annotation { "Feature Type Name" : "Feature", "Feature Type Description" : "" }
export const myFeature = defineFeature(function(context is Context, id is Id, definition is map)
    precondition{}
    {
        {
            var Q0;
            Q0=qCreatedBy(makeId("Top.planeOp"),FACE);
            var sketch = newSketch(context, id + "F0", { "sketchPlane" : qUnion([Q0])});
            skLineSegment(sketch, "E0.bottom", {"start": v(-155.39, 132.34) * mm, "end": v(174.81, 132.34) * mm});
            skLineSegment(sketch, "E0.top", {"start": v(-155.39, -96.26) * mm, "end": v(174.81, -96.26) * mm});
            skLineSegment(sketch, "E0.left", {"start": v(-155.39, 132.34) * mm, "end": v(-155.39, -96.26) * mm});
            skLineSegment(sketch, "E0.right", {"start": v(174.81, 132.34) * mm, "end": v(174.81, -96.26) * mm});
            skCircle(sketch, "E1", {"center": v(-140.15, 117.1) * mm, "radius": 4 * mm});
            skCircle(sketch, "E2", {"center": v(-38.55, 117.1) * mm, "radius": 4 * mm});
            skCircle(sketch, "E3", {"center": v(57.97, 116.69) * mm, "radius": 4 * mm});
            skCircle(sketch, "E4", {"center": v(159.57, 117.1) * mm, "radius": 4 * mm});
            skCircle(sketch, "E5", {"center": v(-140.15, 18.04) * mm, "radius": 4 * mm});
            skCircle(sketch, "E6", {"center": v(-140.15, -58.16) * mm, "radius": 4 * mm});
            skCircle(sketch, "E7", {"center": v(159.57, 18.04) * mm, "radius": 4 * mm});
            skCircle(sketch, "E8", {"center": v(159.57, -58.16) * mm, "radius": 4 * mm});
            skCircle(sketch, "E9", {"center": v(-89.35, -81.02) * mm, "radius": 4 * mm});
            skCircle(sketch, "E10", {"center": v(9.71, -81.02) * mm, "radius": 4.44 * mm});
            skCircle(sketch, "E11", {"center": v(108.77, -81.02) * mm, "radius": 4 * mm});
            skCircle(sketch, "E12", {"center": v(-142.69, -83.56) * mm, "radius": 6.35 * mm});
            skCircle(sketch, "E13", {"center": v(162.11, -83.56) * mm, "radius": 6.35 * mm});
            skText(sketch, "E14", { "text": "CULTUR", "fontName": "RobotoSlab-Regular.ttf"});
            skText(sketch, "E15", { "text": "SUP FISHING", "fontName": "Tinos-Bold.ttf"});
            const initialGuessF0  = {"E14": [-0.08375, 0, 1, 0, 0.02933], "E15": [-0.07246, -0.02336, 1, 0, 0.0163]};
            skSetInitialGuess(sketch, initialGuessF0);
            skSolve(sketch);
        }
        {
            var Q0;
            Q0=makeQuery(id+"F0.imprint","IMPRINT",FACE,{"disambiguationData":[TD([[makeQuery(id+"F0.imprint","IMPRINT",EDGE,{"derivedFrom":sQuery(id+"F0.wireOp",EDGE,"E0.bottom")}),-1.0]])]});
            extrude(context, id + "F1", {"entities" : qUnion([Q0]), "endBound" : BoundingType.SYMMETRIC, "depth" : 12.7 * mm, "offsetDistance" : 25.4 * mm});
        }
        {
            var Q0;
            Q0=makeQuery(id+"F1.opExtrude","SWEPT_EDGE",EDGE,{"disambiguationData":[OSD([sQuery(id+"F0.wireOp",EDGE,"E0.top"),sQuery(id+"F0.wireOp",EDGE,"E0.left")])]});
            var Q1;
            Q1=makeQuery(id+"F1.opExtrude","SWEPT_EDGE",EDGE,{"disambiguationData":[OSD([sQuery(id+"F0.wireOp",EDGE,"E0.top"),sQuery(id+"F0.wireOp",EDGE,"E0.right")])]});
            var Q2;
            Q2=makeQuery(id+"F1.opExtrude","SWEPT_EDGE",EDGE,{"disambiguationData":[OSD([sQuery(id+"F0.wireOp",EDGE,"E0.bottom"),sQuery(id+"F0.wireOp",EDGE,"E0.right")])]});
            var Q3;
            Q3=makeQuery(id+"F1.opExtrude","SWEPT_EDGE",EDGE,{"disambiguationData":[OSD([sQuery(id+"F0.wireOp",EDGE,"E0.bottom"),sQuery(id+"F0.wireOp",EDGE,"E0.left")])]});
            fillet(context, id + "F2", {"entities" : qUnion([Q0, Q1, Q2, Q3]), "radius" : 5.08 * mm, "tangentPropagation" : true, "allowEdgeOverflow" : false});
        }
        {
            var Q0;
            Q0=makeQuery(id+"F1.opExtrude","CAP_EDGE",EDGE,{"disambiguationData":[OSD([sQuery(id+"F0.wireOp",EDGE,"E12")])],"isStart":false});
            var Q1;
            Q1=makeQuery(id+"F1.opExtrude","CAP_EDGE",EDGE,{"disambiguationData":[OSD([sQuery(id+"F0.wireOp",EDGE,"E13")])],"isStart":false});
            chamfer(context, id + "F3", {"entities" : qUnion([Q0, Q1]), "width" : 1.27 * mm, "tangentPropagation" : true});
        }
        {
            var Q0;
            Q0=qCreatedBy(makeId("Front.planeOp"),FACE);
            var sketch = newSketch(context, id + "F4", { "sketchPlane" : qUnion([Q0])});
            skLineSegment(sketch, "E16.bottom", {"start": v(139.7, 89.76) * mm, "end": v(98.1, 89.76) * mm});
            skLineSegment(sketch, "E16.top", {"start": v(139.7, 134.21) * mm, "end": v(-139.7, 134.21) * mm});
            skLineSegment(sketch, "E16.left", {"start": v(139.7, 89.76) * mm, "end": v(139.7, 134.21) * mm});
            skLineSegment(sketch, "E16.right", {"start": v(-139.7, 89.76) * mm, "end": v(-139.7, 134.21) * mm});
            skPoint(sketch, "E16.middle", {"position": v(0, 111.99) * mm});
            skEllipticalArc(sketch, "E17", {});
            skEllipticalArc(sketch, "E18", {});
            skEllipticalArc(sketch, "E19", {});
            skLineSegment(sketch, "E20.trimOffspring", {"start": v(-17.3, 89.76) * mm, "end": v(-71.6, 89.76) * mm});
            skLineSegment(sketch, "E21.trimOffspring", {"start": v(-106.2, 89.76) * mm, "end": v(-139.7, 89.76) * mm});
            skLineSegment(sketch, "E22.trimOffspring", {"start": v(79.7, 89.76) * mm, "end": v(17.3, 89.76) * mm});
            const initialGuessF4  = {"E17": [-0.0889, 0.08976238112449644, 1, 0, 0.017301402986049652, 0.009966931469632298, 0, 3.141592653589793], "E18": [0, 0.08976238112449646, 1, 0, 0.017301402986049652, 0.009966931469632298, 0, 3.141592653589793], "E19": [0.0889, 0.06227371493570839, 1, 0, 0.04859707429410401, 0.027995631886299215, 1.3801990408454565, 1.7613936127443364]};
            skSetInitialGuess(sketch, initialGuessF4);
            skSolve(sketch);
        }
        {
            var Q0;
            Q0 = qSketchRegion(id + "F4", true);
            extrude(context, id + "F5", {"entities" : qUnion([Q0]), "endBound" : BoundingType.SYMMETRIC, "depth" : 12.7 * mm, "offsetDistance" : 25.4 * mm});
        }
        {
            var Q0;
            Q0=makeQuery(id+"F5.opExtrude","SWEPT_EDGE",EDGE,{"disambiguationData":[OSD([sQuery(id+"F4.wireOp",EDGE,"E16.top"),sQuery(id+"F4.wireOp",EDGE,"E16.left")])]});
            var Q1;
            Q1=makeQuery(id+"F5.opExtrude","SWEPT_EDGE",EDGE,{"disambiguationData":[OSD([sQuery(id+"F4.wireOp",EDGE,"E16.top"),sQuery(id+"F4.wireOp",EDGE,"E16.right")])]});
            fillet(context, id + "F6", {"entities" : qUnion([Q0, Q1]), "radius" : 5.08 * mm, "tangentPropagation" : true, "allowEdgeOverflow" : false});
        }
        {
            var Q0;
            Q0=qCreatedBy(makeId("Right.planeOp"),FACE);
            var sketch = newSketch(context, id + "F7", { "sketchPlane" : qUnion([Q0])});
            skLineSegment(sketch, "E23.bottom", {"start": v(-18.2, 30.76) * mm, "end": v(-208.7, 30.76) * mm});
            skLineSegment(sketch, "E23.top", {"start": v(-18.2, 75.21) * mm, "end": v(-208.7, 75.21) * mm});
            skLineSegment(sketch, "E23.left", {"start": v(-18.2, 30.76) * mm, "end": v(-18.2, 75.21) * mm});
            skLineSegment(sketch, "E23.right", {"start": v(-208.7, 30.76) * mm, "end": v(-208.7, 75.21) * mm});
            skPoint(sketch, "E23.middle", {"position": v(-113.46, 52.99) * mm});
            skLineSegment(sketch, "E24.bottom", {"start": v(219.37, 34.23) * mm, "end": v(28.87, 34.23) * mm});
            skLineSegment(sketch, "E24.top", {"start": v(219.37, 78.68) * mm, "end": v(28.87, 78.68) * mm});
            skLineSegment(sketch, "E24.left", {"start": v(219.37, 34.23) * mm, "end": v(219.37, 78.68) * mm});
            skLineSegment(sketch, "E24.right", {"start": v(28.87, 34.23) * mm, "end": v(28.87, 78.68) * mm});
            skPoint(sketch, "E24.middle", {"position": v(124.12, 56.46) * mm});
            skSolve(sketch);
        }
        {
            var Q0;
            Q0=makeQuery(id+"F7.imprint","IMPRINT",FACE,{"disambiguationData":[TD([[makeQuery(id+"F7.imprint","IMPRINT",EDGE,{"derivedFrom":sQuery(id+"F7.wireOp",EDGE,"E23.bottom")}),-1.0]])]});
            var Q1;
            Q1=makeQuery(id+"F7.imprint","IMPRINT",FACE,{"disambiguationData":[TD([[makeQuery(id+"F7.imprint","IMPRINT",EDGE,{"derivedFrom":sQuery(id+"F7.wireOp",EDGE,"E24.bottom")}),-1.0]])]});
            extrude(context, id + "F8", {"entities" : qUnion([Q0, Q1]), "endBound" : BoundingType.SYMMETRIC, "depth" : 12.7 * mm, "offsetDistance" : 25.4 * mm});
        }
        {
            var Q0;
            Q0=makeQuery(id+"F8.opExtrude","SWEPT_EDGE",EDGE,{"disambiguationData":[OSD([sQuery(id+"F7.wireOp",EDGE,"E23.top"),sQuery(id+"F7.wireOp",EDGE,"E23.right")])]});
            var Q1;
            Q1=makeQuery(id+"F8.opExtrude","SWEPT_EDGE",EDGE,{"disambiguationData":[OSD([sQuery(id+"F7.wireOp",EDGE,"E24.top"),sQuery(id+"F7.wireOp",EDGE,"E24.right")])]});
            var Q2;
            Q2=makeQuery(id+"F8.opExtrude","SWEPT_EDGE",EDGE,{"disambiguationData":[OSD([sQuery(id+"F7.wireOp",EDGE,"E24.top"),sQuery(id+"F7.wireOp",EDGE,"E24.left")])]});
            var Q3;
            Q3=makeQuery(id+"F8.opExtrude","SWEPT_EDGE",EDGE,{"disambiguationData":[OSD([sQuery(id+"F7.wireOp",EDGE,"E23.top"),sQuery(id+"F7.wireOp",EDGE,"E23.left")])]});
            fillet(context, id + "F9", {"entities" : qUnion([Q0, Q1, Q2, Q3]), "radius" : 5.08 * mm, "tangentPropagation" : true, "allowEdgeOverflow" : false});
        }
        {
            var Q0;
            Q0=qCreatedBy(makeId("Front.planeOp"),FACE);
            var sketch = newSketch(context, id + "F10", { "sketchPlane" : qUnion([Q0])});
            skLineSegment(sketch, "E25.bottom", {"start": v(139.7, 22.61) * mm, "end": v(-139.7, 22.61) * mm});
            skLineSegment(sketch, "E25.top", {"start": v(139.7, 60.71) * mm, "end": v(-139.7, 60.71) * mm});
            skLineSegment(sketch, "E25.left", {"start": v(139.7, 22.61) * mm, "end": v(139.7, 60.71) * mm});
            skLineSegment(sketch, "E25.right", {"start": v(-139.7, 22.61) * mm, "end": v(-139.7, 60.71) * mm});
            skPoint(sketch, "E25.middle", {"position": v(0, 41.66) * mm});
            skCircle(sketch, "E26", {"center": v(-130.8, 51.19) * mm, "radius": 6.35 * mm});
            skCircle(sketch, "E27", {"center": v(130.8, 51.19) * mm, "radius": 6.35 * mm});
            skSolve(sketch);
        }
        {
            var Q0;
            Q0=makeQuery(id+"F10.imprint","IMPRINT",FACE,{"disambiguationData":[TD([[makeQuery(id+"F10.imprint","IMPRINT",EDGE,{"derivedFrom":sQuery(id+"F10.wireOp",EDGE,"E25.bottom")}),-1.0]])]});
            extrude(context, id + "F11", {"entities" : qUnion([Q0]), "endBound" : BoundingType.SYMMETRIC, "depth" : 12.7 * mm, "offsetDistance" : 25.4 * mm});
        }
        {
            var Q0;
            Q0=makeQuery(id+"F11.opExtrude","SWEPT_EDGE",EDGE,{"disambiguationData":[OSD([sQuery(id+"F10.wireOp",EDGE,"E25.top"),sQuery(id+"F10.wireOp",EDGE,"E25.right")])]});
            var Q1;
            Q1=makeQuery(id+"F11.opExtrude","SWEPT_EDGE",EDGE,{"disambiguationData":[OSD([sQuery(id+"F10.wireOp",EDGE,"E25.top"),sQuery(id+"F10.wireOp",EDGE,"E25.left")])]});
            fillet(context, id + "F12", {"entities" : qUnion([Q0, Q1]), "radius" : 5.08 * mm, "tangentPropagation" : true, "allowEdgeOverflow" : false});
        }
        {
            var Q0;
            Q0=makeQuery(id+"F1.opExtrude","CAP_EDGE",EDGE,{"disambiguationData":[OSD([sQuery(id+"F0.wireOp",EDGE,"E9")])],"isStart":false});
            var Q1;
            Q1=makeQuery(id+"F1.opExtrude","CAP_EDGE",EDGE,{"disambiguationData":[OSD([sQuery(id+"F0.wireOp",EDGE,"E10")])],"isStart":false});
            var Q2;
            Q2=makeQuery(id+"F1.opExtrude","CAP_EDGE",EDGE,{"disambiguationData":[OSD([sQuery(id+"F0.wireOp",EDGE,"E11")])],"isStart":false});
            chamfer(context, id + "F13", {"entities" : qUnion([Q0, Q1, Q2]), "width" : 1.27 * mm, "tangentPropagation" : true});
        }
        {
            var Q0;
            Q0=qCreatedBy(makeId("Front.planeOp"),FACE);
            var sketch = newSketch(context, id + "F14", { "sketchPlane" : qUnion([Q0])});
            skLineSegment(sketch, "E28.bottom", {"start": v(-239.3, -22.25) * mm, "end": v(65.5, -22.25) * mm});
            skLineSegment(sketch, "E28.top", {"start": v(-239.3, -174.65) * mm, "end": v(65.5, -174.65) * mm});
            skLineSegment(sketch, "E28.left", {"start": v(-239.3, -22.25) * mm, "end": v(-239.3, -174.65) * mm});
            skLineSegment(sketch, "E28.right", {"start": v(65.5, -22.25) * mm, "end": v(65.5, -174.65) * mm});
            skEllipse(sketch, "E29", {"center": v(-86.9, -140.84) * mm, "majorRadius": 44.45 * mm, "minorRadius": 7.62 * mm, "majorAxis": v(1, 0)});
            skLineSegment(sketch, "E30", {"start": v(200.61, 72.88) * mm, "end": v(200.61, 98.28) * mm});
            skLineSegment(sketch, "E31", {"start": v(226.01, 98.28) * mm, "end": v(200.61, 98.28) * mm});
            skLineSegment(sketch, "E32", {"start": v(420.88, 105.63) * mm, "end": v(420.88, 131.03) * mm});
            skLineSegment(sketch, "E33", {"start": v(446.28, 131.03) * mm, "end": v(420.88, 131.03) * mm});
            skLineSegment(sketch, "E34", {"start": v(230.3, -8.4) * mm, "end": v(230.3, 17) * mm});
            skLineSegment(sketch, "E35", {"start": v(255.7, 17) * mm, "end": v(230.3, 17) * mm});
            skLineSegment(sketch, "E36", {"start": v(245.03, 105.41) * mm, "end": v(245.03, 130.81) * mm});
            skLineSegment(sketch, "E37", {"start": v(270.43, 130.81) * mm, "end": v(245.03, 130.81) * mm});
            skLineSegment(sketch, "E38", {"start": v(243.4, -68.18) * mm, "end": v(243.4, -42.78) * mm});
            skLineSegment(sketch, "E39", {"start": v(268.8, -42.78) * mm, "end": v(243.4, -42.78) * mm});
            skSolve(sketch);
        }
        {
            var Q0;
            Q0=makeQuery(id+"F14.imprint","IMPRINT",FACE,{"disambiguationData":[TD([[makeQuery(id+"F14.imprint","IMPRINT",EDGE,{"derivedFrom":sQuery(id+"F14.wireOp",EDGE,"E28.bottom")}),-1.0]])]});
            extrude(context, id + "F15", {"entities" : qUnion([Q0]), "endBound" : BoundingType.SYMMETRIC, "depth" : 6.35 * mm, "offsetDistance" : 25.4 * mm});
        }
        {
            var Q0;
            Q0=makeQuery(id+"F15.opExtrude","SWEPT_EDGE",EDGE,{"disambiguationData":[OSD([sQuery(id+"F14.wireOp",EDGE,"E28.bottom"),sQuery(id+"F14.wireOp",EDGE,"E28.left")])]});
            var Q1;
            Q1=makeQuery(id+"F15.opExtrude","SWEPT_EDGE",EDGE,{"disambiguationData":[OSD([sQuery(id+"F14.wireOp",EDGE,"E28.top"),sQuery(id+"F14.wireOp",EDGE,"E28.left")])]});
            var Q2;
            Q2=makeQuery(id+"F15.opExtrude","SWEPT_EDGE",EDGE,{"disambiguationData":[OSD([sQuery(id+"F14.wireOp",EDGE,"E28.top"),sQuery(id+"F14.wireOp",EDGE,"E28.right")])]});
            var Q3;
            Q3=makeQuery(id+"F15.opExtrude","SWEPT_EDGE",EDGE,{"disambiguationData":[OSD([sQuery(id+"F14.wireOp",EDGE,"E28.bottom"),sQuery(id+"F14.wireOp",EDGE,"E28.right")])]});
            fillet(context, id + "F16", {"entities" : qUnion([Q0, Q1, Q2, Q3]), "radius" : 5.08 * mm, "tangentPropagation" : true, "allowEdgeOverflow" : false});
        }
        {
            var Q0;
            Q0=qCreatedBy(makeId("Front.planeOp"),FACE);
            var sketch = newSketch(context, id + "F17", { "sketchPlane" : qUnion([Q0])});
            skLineSegment(sketch, "E40.bottom", {"start": v(100.89, -44.58) * mm, "end": v(108.51, -44.58) * mm});
            skLineSegment(sketch, "E40.top", {"start": v(100.89, -146.18) * mm, "end": v(108.51, -146.18) * mm});
            skLineSegment(sketch, "E40.left", {"start": v(100.89, -44.58) * mm, "end": v(100.89, -146.18) * mm});
            skLineSegment(sketch, "E40.right", {"start": v(108.51, -44.58) * mm, "end": v(108.51, -146.18) * mm});
            skLineSegment(sketch, "E41.bottom", {"start": v(132.19, -47.24) * mm, "end": v(139.8, -47.24) * mm});
            skLineSegment(sketch, "E41.top", {"start": v(132.19, -148.84) * mm, "end": v(139.8, -148.84) * mm});
            skLineSegment(sketch, "E41.left", {"start": v(132.19, -47.24) * mm, "end": v(132.19, -148.84) * mm});
            skLineSegment(sketch, "E41.right", {"start": v(139.8, -47.24) * mm, "end": v(139.8, -148.84) * mm});
            skSolve(sketch);
        }
        {
            var Q0;
            Q0 = qSketchRegion(id + "F17", true);
            extrude(context, id + "F18", {"entities" : qUnion([Q0]), "depth" : 2.03 * mm, "offsetDistance" : 25.4 * mm});
        }
        {
            var Q0;
            Q0=makeQuery(id+"F18.opExtrude","SWEPT_FACE",FACE,{"disambiguationData":[OSD([sQuery(id+"F17.wireOp",EDGE,"E40.right")])]});
            var sketch = newSketch(context, id + "F19", { "sketchPlane" : qUnion([Q0])});
            skLineSegment(sketch, "E42", {"start": v(0, -146.18) * mm, "end": v(7.62, -146.18) * mm});
            skLineSegment(sketch, "E43", {"start": v(0, -44.58) * mm, "end": v(7.62, -44.58) * mm});
            skLineSegment(sketch, "E44", {"start": v(7.62, -44.58) * mm, "end": v(7.62, -146.18) * mm});
            skSolve(sketch);
        }
        {
            var Q0;
            Q0=makeQuery(id+"F19.imprint","IMPRINT",FACE,{"disambiguationData":[TD([[makeQuery(id+"F19.imprint","IMPRINT",EDGE,{"derivedFrom":sQuery(id+"F19.wireOp",EDGE,"E42")}),1.0]])]});
            extrude(context, id + "F20", {"entities" : qUnion([Q0]), "operationType" : NewBodyOperationType.ADD, "endBound" : BoundingType.SYMMETRIC, "depth" : 0.5 * mm, "offsetDistance" : 25.4 * mm});
        }
        {
            var Q0;
            Q0=makeQuery(id+"F18.opExtrude","SWEPT_FACE",FACE,{"disambiguationData":[OSD([sQuery(id+"F17.wireOp",EDGE,"E41.right")])]});
            var sketch = newSketch(context, id + "F21", { "sketchPlane" : qUnion([Q0])});
            skLineSegment(sketch, "E45", {"start": v(0, -148.84) * mm, "end": v(7.62, -148.84) * mm});
            skLineSegment(sketch, "E46", {"start": v(0, -47.24) * mm, "end": v(7.62, -47.24) * mm});
            skLineSegment(sketch, "E47", {"start": v(7.62, -47.24) * mm, "end": v(7.62, -148.84) * mm});
            skSolve(sketch);
        }
        {
            var Q0;
            Q0=makeQuery(id+"F21.imprint","IMPRINT",FACE,{"disambiguationData":[TD([[makeQuery(id+"F21.imprint","IMPRINT",EDGE,{"derivedFrom":sQuery(id+"F21.wireOp",EDGE,"E45")}),1.0]])]});
            extrude(context, id + "F22", {"entities" : qUnion([Q0]), "operationType" : NewBodyOperationType.ADD, "endBound" : BoundingType.SYMMETRIC, "depth" : 0.5 * mm, "offsetDistance" : 25.4 * mm});
        }
    });